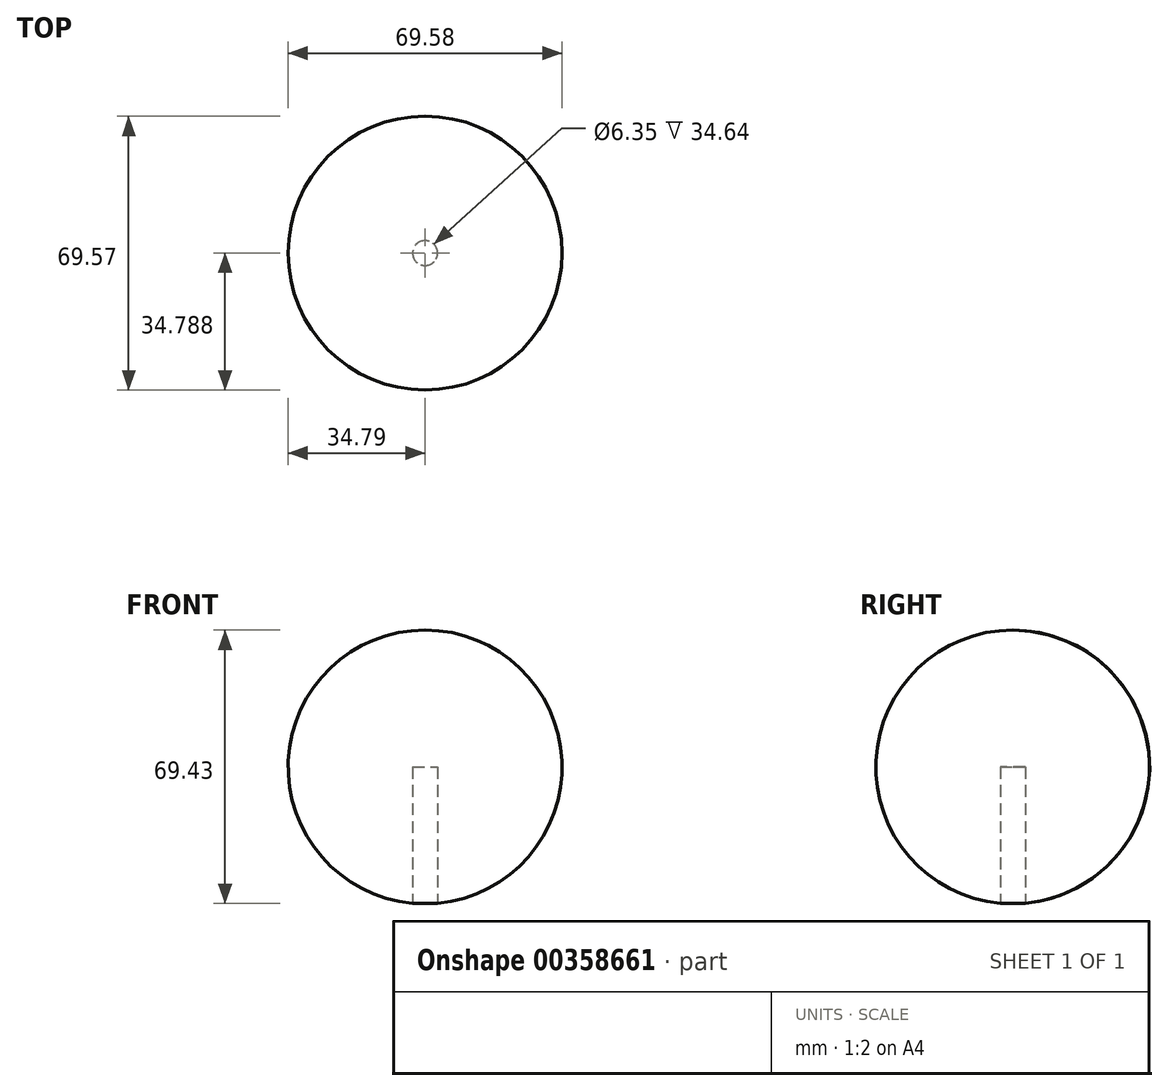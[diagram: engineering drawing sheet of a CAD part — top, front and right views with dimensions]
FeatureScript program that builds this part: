
annotation { "Feature Type Name" : "Feature", "Feature Type Description" : "" }
export const myFeature = defineFeature(function(context is Context, id is Id, definition is map)
    precondition{}
    {
        {
            var Q0;
            Q0=qCreatedBy(makeId("Right.planeOp"),FACE);
            var sketch = newSketch(context, id + "F0", { "sketchPlane" : qUnion([Q0])});
            skLineSegment(sketch, "E0", {"start": v(-39.08, 87.76) * mm, "end": v(-42.26, 87.76) * mm});
            skLineSegment(sketch, "E1", {"start": v(-42.26, 87.76) * mm, "end": v(-42.26, 53.12) * mm});
            skArc(sketch, "E2", {"start": v(-39.08, 122.55) * mm, "mid": v(-73.83, 89.35) * mm, "end": v(-42.26, 53.12) * mm});
            skLineSegment(sketch, "E3", {"start": v(-39.08, 87.76) * mm, "end": v(-39.08, 122.55) * mm});
            skSolve(sketch);
        }
        {
            var Q0;
            Q0=makeQuery(id+"F0.imprint","IMPRINT",FACE,{"disambiguationData":[TD([[makeQuery(id+"F0.imprint","IMPRINT",EDGE,{"derivedFrom":sQuery(id+"F0.wireOp",EDGE,"E0")}),-1.0]])]});
            var Q1;
            Q1=sQuery(id+"F0.wireOp",EDGE,"E3");
            revolve(context, id + "F1", {"entities" : qUnion([Q0]), "axis" : qUnion([Q1]), "revolveType" : RevolveType.FULL});
        }
    });
